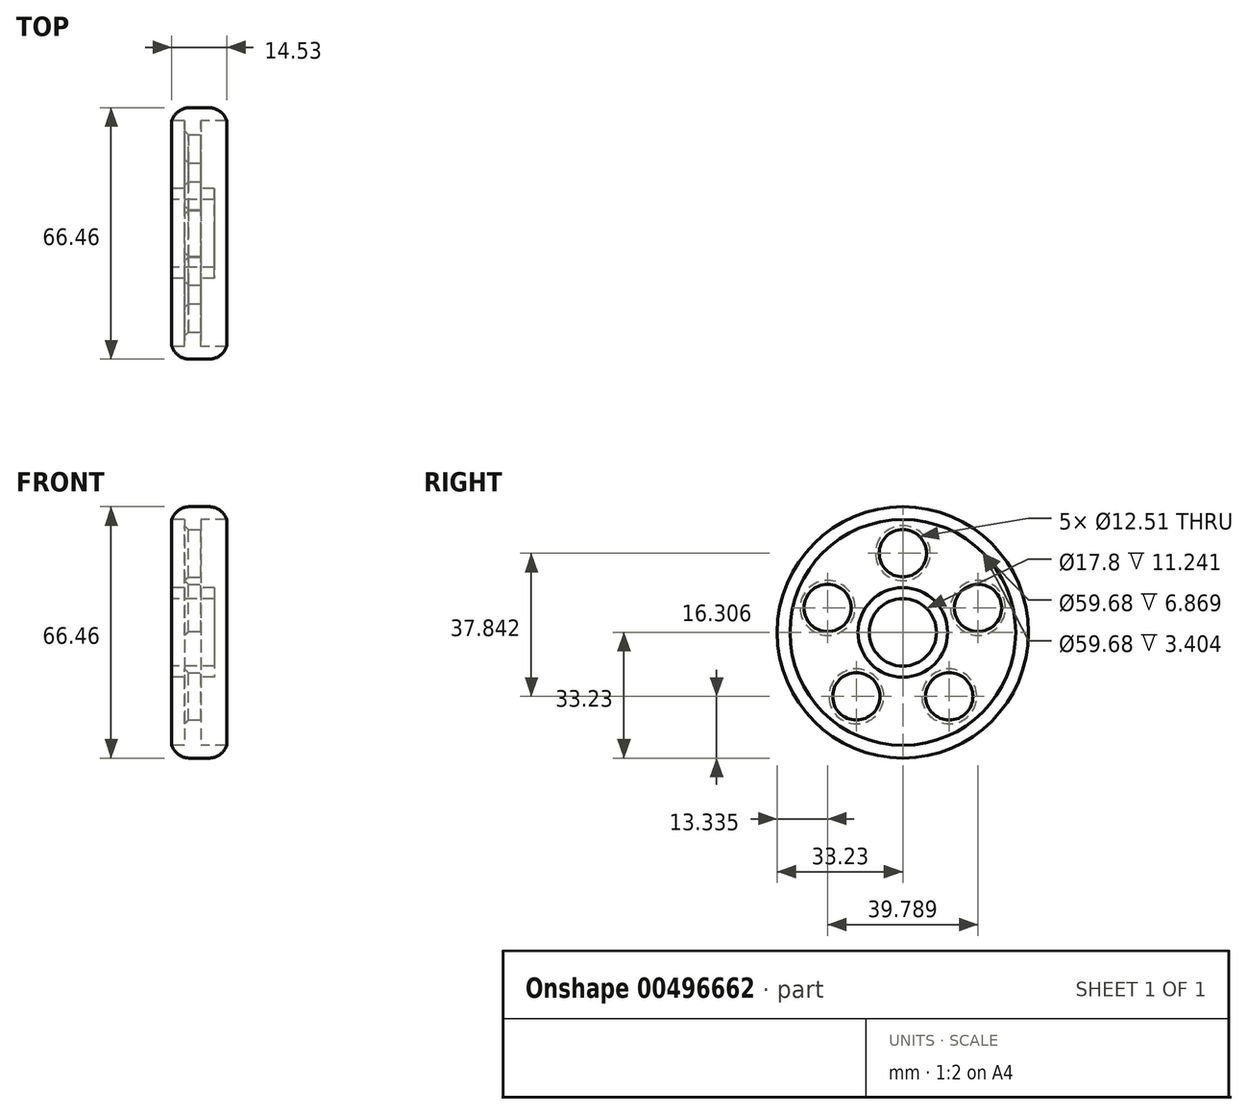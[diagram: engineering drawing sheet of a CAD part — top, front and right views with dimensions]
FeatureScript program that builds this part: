
annotation { "Feature Type Name" : "Feature", "Feature Type Description" : "" }
export const myFeature = defineFeature(function(context is Context, id is Id, definition is map)
    precondition{}
    {
        {
            var Q0;
            Q0=qCreatedBy(makeId("Front.planeOp"),FACE);
            var sketch = newSketch(context, id + "F0", { "sketchPlane" : qUnion([Q0])});
            skLineSegment(sketch, "E0", {"start": v(0, 8.9) * mm, "end": v(11.24, 8.9) * mm});
            skLineSegment(sketch, "E1", {"start": v(11.24, 8.9) * mm, "end": v(11.24, 11.84) * mm});
            skLineSegment(sketch, "E2", {"start": v(11.24, 11.84) * mm, "end": v(7.66, 11.84) * mm});
            skLineSegment(sketch, "E3", {"start": v(7.66, 11.84) * mm, "end": v(7.66, 29.84) * mm});
            skLineSegment(sketch, "E4", {"start": v(7.66, 29.84) * mm, "end": v(14.53, 29.84) * mm});
            skLineSegment(sketch, "E5", {"start": v(14.53, 29.84) * mm, "end": v(14.53, 33.23) * mm});
            skLineSegment(sketch, "E6", {"start": v(14.53, 33.23) * mm, "end": v(0, 33.23) * mm});
            skLineSegment(sketch, "E7", {"start": v(0, 33.23) * mm, "end": v(0, 29.84) * mm});
            skLineSegment(sketch, "E8", {"start": v(0, 29.84) * mm, "end": v(3.4, 29.84) * mm});
            skLineSegment(sketch, "E9", {"start": v(3.4, 29.84) * mm, "end": v(3.4, 11.84) * mm});
            skLineSegment(sketch, "E10", {"start": v(3.4, 11.84) * mm, "end": v(0, 11.84) * mm});
            skLineSegment(sketch, "E11", {"start": v(0, 11.84) * mm, "end": v(0, 8.9) * mm});
            skLineSegment(sketch, "E12", {"start": v(0, 0) * mm, "end": v(14.9, 0) * mm});
            skSolve(sketch);
        }
        {
            var Q0;
            Q0 = qSketchRegion(id + "F0", true);
            var Q1;
            Q1=sQuery(id+"F0.wireOp",EDGE,"E12");
            revolve(context, id + "F1", {"entities" : qUnion([Q0]), "axis" : qUnion([Q1]), "revolveType" : RevolveType.FULL});
        }
        {
            var Q0;
            Q0=makeQuery(id+"F1.opRevolve","SWEPT_FACE",FACE,{"disambiguationData":[OSD([sQuery(id+"F0.wireOp",EDGE,"E3")])]});
            var sketch = newSketch(context, id + "F2", { "sketchPlane" : qUnion([Q0])});
            skCircle(sketch, "E13", {"center": v(0, 20.92) * mm, "radius": 6.26 * mm});
            skCircle(sketch, "E14.1.0", {"center": v(-19.9, 6.46) * mm, "radius": 6.26 * mm});
            skCircle(sketch, "E14.2.0", {"center": v(-12.3, -16.92) * mm, "radius": 6.26 * mm});
            skCircle(sketch, "E14.3.0", {"center": v(12.3, -16.92) * mm, "radius": 6.26 * mm});
            skCircle(sketch, "E14.4.0", {"center": v(19.9, 6.46) * mm, "radius": 6.26 * mm});
            skPoint(sketch, "E14.center", {"position": v(0, 0) * mm});
            skSolve(sketch);
        }
        {
            var Q0;
            Q0=makeQuery(id+"F2.imprint","IMPRINT",FACE,{"disambiguationData":[TD([[makeQuery(id+"F2.imprint","IMPRINT",EDGE,{"derivedFrom":sQuery(id+"F2.wireOp",EDGE,"E13")}),1.0]])]});
            var Q1;
            Q1=makeQuery(id+"F2.imprint","IMPRINT",FACE,{"disambiguationData":[TD([[makeQuery(id+"F2.imprint","IMPRINT",EDGE,{"derivedFrom":sQuery(id+"F2.wireOp",EDGE,"E14.4.0")}),1.0]])]});
            var Q2;
            Q2=makeQuery(id+"F2.imprint","IMPRINT",FACE,{"disambiguationData":[TD([[makeQuery(id+"F2.imprint","IMPRINT",EDGE,{"derivedFrom":sQuery(id+"F2.wireOp",EDGE,"E14.3.0")}),1.0]])]});
            var Q3;
            Q3=makeQuery(id+"F2.imprint","IMPRINT",FACE,{"disambiguationData":[TD([[makeQuery(id+"F2.imprint","IMPRINT",EDGE,{"derivedFrom":sQuery(id+"F2.wireOp",EDGE,"E14.2.0")}),1.0]])]});
            var Q4;
            Q4=makeQuery(id+"F2.imprint","IMPRINT",FACE,{"disambiguationData":[TD([[makeQuery(id+"F2.imprint","IMPRINT",EDGE,{"derivedFrom":sQuery(id+"F2.wireOp",EDGE,"E14.1.0")}),1.0]])]});
            extrude(context, id + "F3", {"entities" : qUnion([Q0, Q1, Q2, Q3, Q4]), "operationType" : NewBodyOperationType.REMOVE, "oppositeDirection" : true, "depth" : 25 * mm});
        }
        {
            var Q0;
            Q0=makeQuery(id+"F1.opRevolve","SWEPT_EDGE",EDGE,{"disambiguationData":[OSD([sQuery(id+"F0.wireOp",EDGE,"E5"),sQuery(id+"F0.wireOp",EDGE,"E6")])]});
            var Q1;
            Q1=makeQuery(id+"F1.opRevolve","SWEPT_EDGE",EDGE,{"disambiguationData":[OSD([sQuery(id+"F0.wireOp",EDGE,"E6"),sQuery(id+"F0.wireOp",EDGE,"E7")])]});
            var Q2;
            Q2=makeQuery(id+"F1.opRevolve","SWEPT_FACE",FACE,{"disambiguationData":[OSD([sQuery(id+"F0.wireOp",EDGE,"E6")])]});
            fillet(context, id + "F4", {"entities" : qUnion([Q0, Q1, Q2]), "radius" : 5 * mm, "tangentPropagation" : true, "allowEdgeOverflow" : false});
        }
        {
            var Q0;
            Q0=makeQuery(id+"F3.boolean.opBoolean","INTERSECT",EDGE,{"derivedFrom":[makeQuery(id+"F1.opRevolve","SWEPT_FACE",FACE,{"disambiguationData":[OSD([sQuery(id+"F0.wireOp",EDGE,"E9")])]}),makeQuery(id+"F3.opExtrude","SWEPT_FACE",FACE,{"disambiguationData":[OSD([sQuery(id+"F2.wireOp",EDGE,"E13")])]})]});
            var Q1;
            Q1=makeQuery(id+"F3.boolean.opBoolean","INTERSECT",EDGE,{"derivedFrom":[makeQuery(id+"F1.opRevolve","SWEPT_FACE",FACE,{"disambiguationData":[OSD([sQuery(id+"F0.wireOp",EDGE,"E9")])]}),makeQuery(id+"F3.opExtrude","SWEPT_FACE",FACE,{"disambiguationData":[OSD([sQuery(id+"F2.wireOp",EDGE,"E14.1.0")])]})]});
            var Q2;
            Q2=makeQuery(id+"F3.boolean.opBoolean","INTERSECT",EDGE,{"derivedFrom":[makeQuery(id+"F1.opRevolve","SWEPT_FACE",FACE,{"disambiguationData":[OSD([sQuery(id+"F0.wireOp",EDGE,"E9")])]}),makeQuery(id+"F3.opExtrude","SWEPT_FACE",FACE,{"disambiguationData":[OSD([sQuery(id+"F2.wireOp",EDGE,"E14.2.0")])]})]});
            var Q3;
            Q3=makeQuery(id+"F3.boolean.opBoolean","INTERSECT",EDGE,{"derivedFrom":[makeQuery(id+"F1.opRevolve","SWEPT_FACE",FACE,{"disambiguationData":[OSD([sQuery(id+"F0.wireOp",EDGE,"E9")])]}),makeQuery(id+"F3.opExtrude","SWEPT_FACE",FACE,{"disambiguationData":[OSD([sQuery(id+"F2.wireOp",EDGE,"E14.3.0")])]})]});
            var Q4;
            Q4=makeQuery(id+"F3.boolean.opBoolean","INTERSECT",EDGE,{"derivedFrom":[makeQuery(id+"F1.opRevolve","SWEPT_FACE",FACE,{"disambiguationData":[OSD([sQuery(id+"F0.wireOp",EDGE,"E9")])]}),makeQuery(id+"F3.opExtrude","SWEPT_FACE",FACE,{"disambiguationData":[OSD([sQuery(id+"F2.wireOp",EDGE,"E14.4.0")])]})]});
            chamfer(context, id + "F5", {"entities" : qUnion([Q0, Q1, Q2, Q3, Q4]), "width" : 1 * mm, "tangentPropagation" : true});
        }
    });
